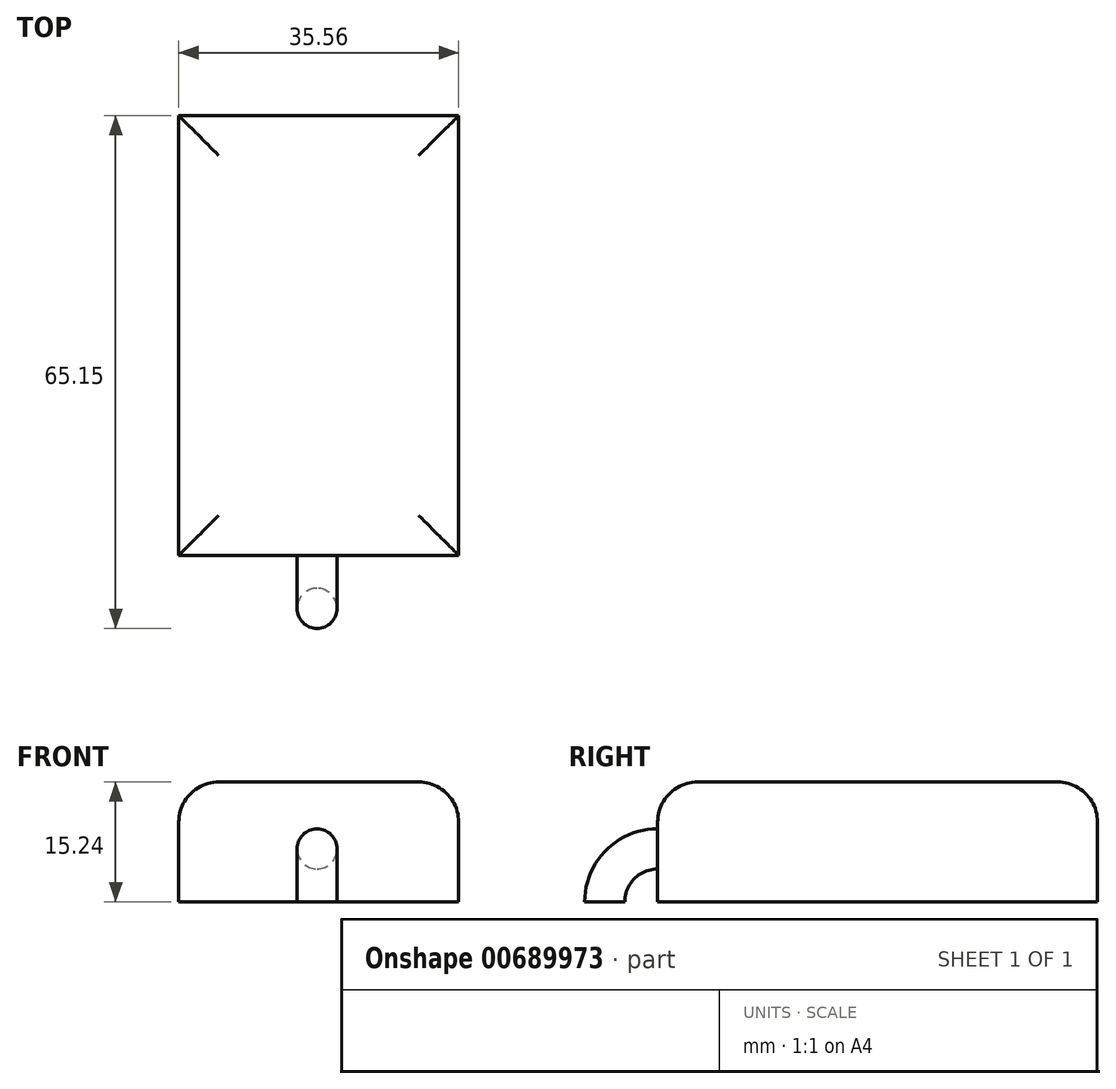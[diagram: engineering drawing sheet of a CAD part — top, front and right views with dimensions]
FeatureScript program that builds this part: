
annotation { "Feature Type Name" : "Feature", "Feature Type Description" : "" }
export const myFeature = defineFeature(function(context is Context, id is Id, definition is map)
    precondition{}
    {
        {
            var Q0;
            Q0=qCreatedBy(makeId("Top.planeOp"),FACE);
            var sketch = newSketch(context, id + "F0", { "sketchPlane" : qUnion([Q0])});
            skLineSegment(sketch, "E0.bottom", {"start": v(-45.02, 29.17) * mm, "end": v(-9.46, 29.17) * mm});
            skLineSegment(sketch, "E0.top", {"start": v(-45.02, -26.7) * mm, "end": v(-9.46, -26.7) * mm});
            skLineSegment(sketch, "E0.left", {"start": v(-45.02, 29.17) * mm, "end": v(-45.02, -26.7) * mm});
            skLineSegment(sketch, "E0.right", {"start": v(-9.46, 29.17) * mm, "end": v(-9.46, -26.7) * mm});
            skSolve(sketch);
        }
        {
            var Q0;
            Q0=makeQuery(id+"F0.imprint","IMPRINT",FACE,{"disambiguationData":[TD([[makeQuery(id+"F0.imprint","IMPRINT",EDGE,{"derivedFrom":sQuery(id+"F0.wireOp",EDGE,"E0.bottom")}),-1.0]])]});
            extrude(context, id + "F1", {"entities" : qUnion([Q0]), "depth" : 15.24 * mm, "offsetDistance" : 25.4 * mm});
        }
        {
            var Q0;
            Q0=makeQuery(id+"F1.opExtrude","CAP_FACE",FACE,{"disambiguationData":[OSD([sQuery(id+"F0.wireOp",EDGE,"E0.bottom"),sQuery(id+"F0.wireOp",EDGE,"E0.top"),sQuery(id+"F0.wireOp",EDGE,"E0.left"),sQuery(id+"F0.wireOp",EDGE,"E0.right")])],"isStart":false});
            fillet(context, id + "F2", {"entities" : qUnion([Q0]), "radius" : 5.08 * mm, "tangentPropagation" : true, "allowEdgeOverflow" : false});
        }
        {
            var Q0;
            Q0=makeQuery(id+"F1.opExtrude","SWEPT_FACE",FACE,{"disambiguationData":[OSD([sQuery(id+"F0.wireOp",EDGE,"E0.top")])]});
            var sketch = newSketch(context, id + "F3", { "sketchPlane" : qUnion([Q0])});
            skCircle(sketch, "E1", {"center": v(-27.45, 6.73) * mm, "radius": 2.55 * mm});
            skSolve(sketch);
        }
        {
            var Q0;
            Q0=makeQuery(id+"F3.imprint","IMPRINT",FACE,{"disambiguationData":[TD([[makeQuery(id+"F3.imprint","IMPRINT",EDGE,{"derivedFrom":sQuery(id+"F3.wireOp",EDGE,"E1")}),1.0]])]});
            var Q1;
            Q1=makeQuery(id+"F1.opExtrude","CAP_EDGE",EDGE,{"disambiguationData":[OSD([sQuery(id+"F0.wireOp",EDGE,"E0.top")])],"isStart":true});
            revolve(context, id + "F4", {"operationType" : NewBodyOperationType.ADD, "entities" : qUnion([Q0]), "axis" : qUnion([Q1]), "revolveType" : RevolveType.ONE_DIRECTION, "angle" : 90 * degree});
        }
    });
